# Revit family: Hager-Vector-IP55-sistema-NoHosted-PT-pt
name_source: partatom
category: Electrical Equipment
units: mm (PartAtom-declared; Revit-internal decimal feet)

## family parameters
Always vertical = Yes
Cut with Voids When Loaded = No
Panel Configuration = Two Columns, Circuits Across
Part Type = Panelboard
Room Calculation Point = No
Round Connector Dimension = Use Diameter
Shared = No
Work Plane-Based = Yes

## types (10) — shared parameters
Default Elevation = 1219 mm
EF000003 - Método de montagem = EV000384 - Montagem em superfície (gesso)
EF000007 - Cor = EV000270 - Cinzento
EF000116 - Número RAL = 7035
EF000118 - Com tampa de montagem = No
EF000339 - Tipo de difusor = EV004216 - Porta
EF001062 - Versão EMC = No
EF001088 - Extensão possível = Yes
EF001134 - Calha DIN = Yes
EF001596 - Material do corpo = EV000139 - Plástico
EF004462 - Tipo de fecho = EV000154 - Outro
EF005474 - Grau de proteção (IP) = EV006421 - IP65
EF006244 - Tampa/porta transparente = No
EF006306 - Com fecho = No
EF009212 - Tipo de tampa = EV000116 - Fechado
EF015776 - Borne de terra = No
EF015777 - Borne de neutro = No
EF015941 - Porta para passagem de sinal = Yes
HG000001 - Número de colunas = 1
HG000002 - Com porta ou tampa = Yes
HG000003 - Gama = Vector
HG000005 - Espessura = 3 mm  [stored 0.00984252 ft]
HG000006 - Encastrado = No
HG000009 - Porta dupla = No
HG000010 - Portas assimétricas = No
HG000011 - Filas vazias desde da parte de baixo = No
HG000017 - Distância entre polos = 18 mm  [stored 0.0590551 ft]
Manufacturer = Hager
Type Comments = Vector
zero-valued in all types: EF000218 - Profundidade incorporada, EF000332 - Altura embutida, EF000846 - Largura para embutir, HG000007 - Número de colunas vazias, HG000008 - Número de filas vazias

## per-type parameters (varying)
| type | EF000008 - Largura | EF000040 - Altura | EF000049 - Profundidade | EF000266 - Número de linhas | EF001131 - Profundidade interior | EF002950 - Largura em número de módulos | HG000004 - Referência do Fabricante | Model |
| Montagem em superfície IP65 L111 A175 P93 3 unidade de divisão - VE103F | 111 mm | 175 mm | 93 mm | 1 | 93 mm | 3 | VE103F | VE103F |
| Montagem em superfície IP65 L165 A190 P113 6 unidade de divisão - VE106F | 165 mm | 190 mm | 113 mm | 1 | 113 mm | 6 | VE106F | VE106F |
| Montagem em superfície IP65 L237 A210 P114 10 unidade de divisão - VE110F | 237 mm | 210 mm | 114 mm | 1 | 114 mm | 10 | VE110F | VE110F |
| Montagem em superfície IP65 L310 A302 P151 12 unidade de divisão - VE112F | 310 mm | 302 mm | 151 mm  [stored 0.495407 ft] | 1 | 151 mm  [stored 0.495407 ft] | 12 | VE112F | VE112F |
| Montagem em superfície IP65 L310 A427 P151 12 unidade de divisão - VE212F | 310 mm | 427 mm | 151 mm  [stored 0.495407 ft] | 2 | 151 mm  [stored 0.495407 ft] | 12 | VE212F | VE212F |
| Montagem em superfície IP65 L310 A552 P151 12 unidade de divisão - VE312F | 310 mm | 552 mm | 151 mm  [stored 0.495407 ft] | 3 | 151 mm  [stored 0.495407 ft] | 12 | VE312F | VE312F |
| Montagem em superfície IP65 L310 A677 P151 12 unidade de divisão - VE412F | 310 mm | 677 mm | 151 mm  [stored 0.495407 ft] | 4 | 151 mm  [stored 0.495407 ft] | 12 | VE412F | VE412F |
| Montagem em superfície IP65 L418 A302 P151 18 unidade de divisão - VE118F | 418 mm  [stored 1.37139 ft] | 302 mm | 151 mm  [stored 0.495407 ft] | 1 | 151 mm  [stored 0.495407 ft] | 18 | VE118F | VE118F |
| Montagem em superfície IP65 L418 A452 P151 18 unidade de divisão - VE218F | 418 mm  [stored 1.37139 ft] | 452 mm | 151 mm  [stored 0.495407 ft] | 2 | 151 mm  [stored 0.495407 ft] | 18 | VE218F | VE218F |
| Montagem em superfície IP65 L418 A602 P151 18 unidade de divisão - VE318F | 418 mm  [stored 1.37139 ft] | 602 mm  [stored 1.97507 ft] | 151 mm  [stored 0.495407 ft] | 3 | 151 mm  [stored 0.495407 ft] | 18 | VE318F | VE318F |

note: [stored X ft] marks values corroborated as IEEE doubles in the binary element streams (Revit-internal decimal feet)

## geometry (parser evidence)
native form markers: Sweep x13
no freeform markers — native parametric forms only
